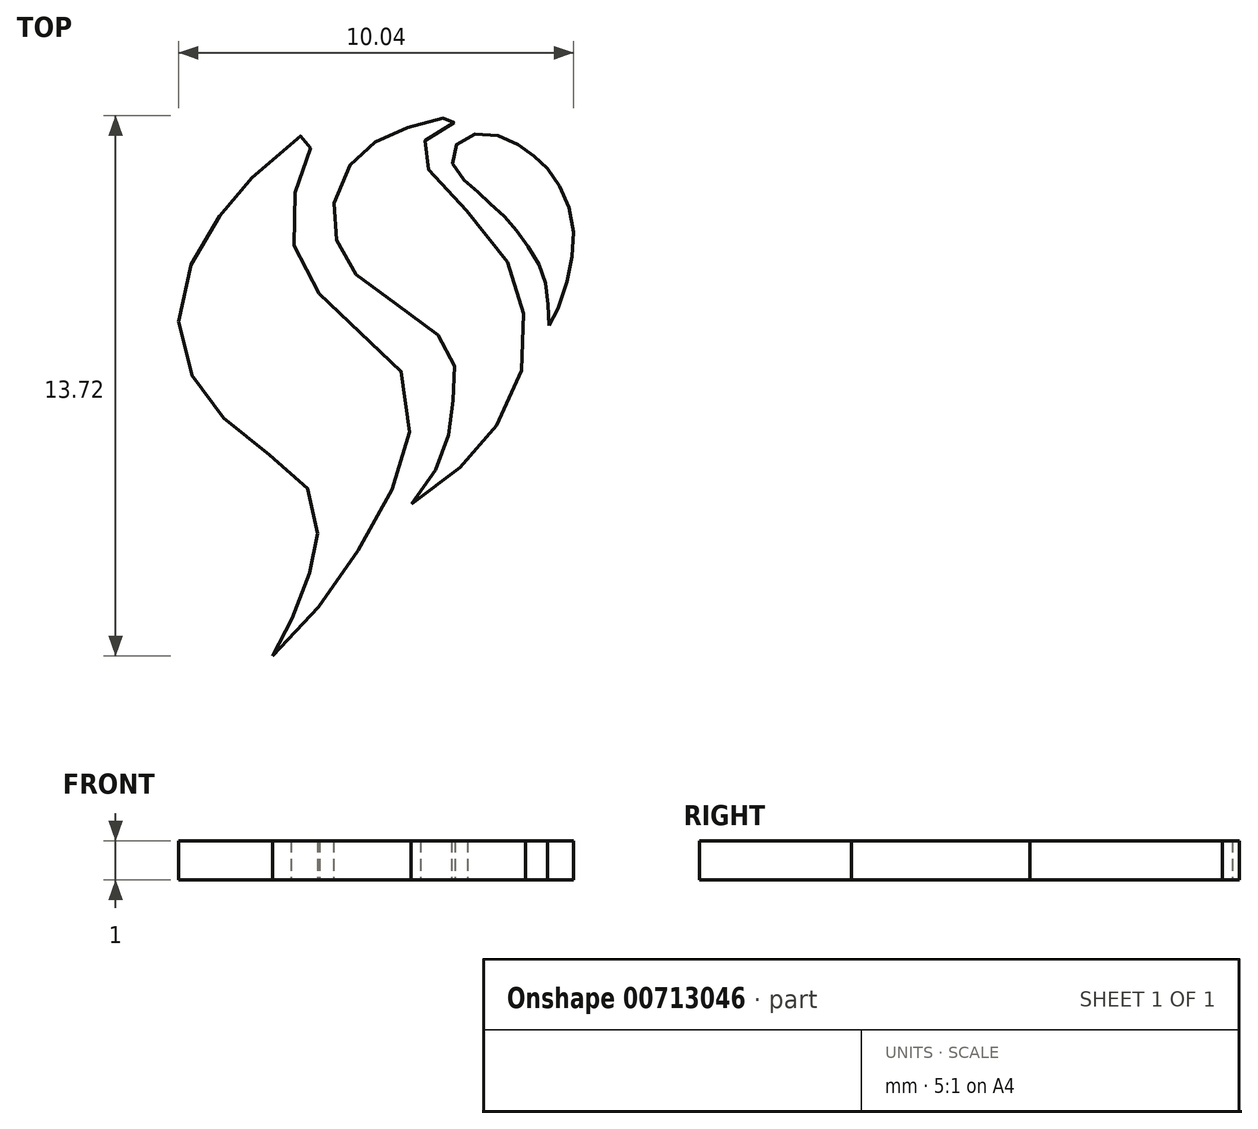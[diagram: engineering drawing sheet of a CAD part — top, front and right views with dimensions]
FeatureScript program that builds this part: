
annotation { "Feature Type Name" : "Feature", "Feature Type Description" : "" }
export const myFeature = defineFeature(function(context is Context, id is Id, definition is map)
    precondition{}
    {
        {
            var Q0;
            Q0=qCreatedBy(makeId("Top.planeOp"),FACE);
            var sketch = newSketch(context, id + "F0", { "sketchPlane" : qUnion([Q0])});
            skFitSpline(sketch, "E0", {"points": [v(-1.7, -8.38) * mm, v(-1.5, -8.04) * mm, v(-1.34, -7.68) * mm, v(-1.1, -7.2) * mm, v(-0.86, -6.51) * mm, v(-0.77, -6.27) * mm, v(-0.66, -5.92) * mm, v(-0.58, -5.52) * mm, v(-0.56, -5.15) * mm, v(-0.6, -4.61) * mm, v(-0.8, -4.16) * mm, v(-1.21, -3.7) * mm, v(-1.66, -3.36) * mm, v(-2.33, -2.9) * mm, v(-2.92, -2.38) * mm, v(-3.34, -1.9) * mm, v(-3.72, -1.33) * mm, v(-3.96, -0.8) * mm, v(-4.1, 0) * mm, v(-4.04, 0.84) * mm, v(-3.77, 1.58) * mm, v(-3.4, 2.33) * mm, v(-3.04, 2.82) * mm, v(-2.69, 3.24) * mm, v(-2.27, 3.72) * mm, v(-1.86, 4.11) * mm, v(-0.9, 4.9) * mm, v(-0.52, 5.14) * mm, v(-0.7, 4.61) * mm, v(-0.85, 4.23) * mm, v(-1.07, 3.65) * mm, v(-1.18, 3.15) * mm, v(-1.23, 2.49) * mm, v(-1.08, 1.76) * mm, v(-0.8, 1.16) * mm, v(-0.35, 0.63) * mm, v(0.08, 0.16) * mm, v(0.83, -0.38) * mm, v(1.32, -0.81) * mm, v(1.73, -1.55) * mm, v(1.8, -2.43) * mm, v(1.63, -3.32) * mm, v(1.36, -4.06) * mm, v(0.88, -5) * mm, v(0.28, -5.99) * mm, v(-0.32, -6.84) * mm, v(-1.24, -7.97) * mm, v(-1.7, -8.38) * mm]});
            skFitSpline(sketch, "E1", {"points": [v(1.82, -4.52) * mm, v(2.2, -4.06) * mm, v(2.43, -3.65) * mm, v(2.6, -3.25) * mm, v(2.74, -2.83) * mm, v(2.8, -2.53) * mm, v(2.85, -2.15) * mm, v(2.9, -1.7) * mm, v(2.9, -1.27) * mm, v(2.92, -1) * mm, v(2.78, -0.64) * mm, v(2.55, -0.3) * mm, v(2.25, 0) * mm, v(1.32, 0.63) * mm, v(0.69, 1.05) * mm, v(0.26, 1.5) * mm, v(0.01, 1.96) * mm, v(-0.11, 2.27) * mm, v(-0.16, 2.72) * mm, v(-0.14, 3.15) * mm, v(0, 3.72) * mm, v(0.28, 4.11) * mm, v(0.5, 4.34) * mm, v(0.82, 4.61) * mm, v(1.09, 4.78) * mm, v(1.54, 4.96) * mm, v(1.8, 5.07) * mm, v(2.32, 5.2) * mm, v(2.65, 5.28) * mm, v(3.24, 5.33) * mm, v(2.93, 5.19) * mm, v(2.57, 5) * mm, v(2.28, 4.8) * mm, v(2.08, 4.6) * mm, v(2.07, 4.27) * mm, v(2.25, 3.98) * mm, v(2.6, 3.55) * mm, v(3.7, 2.44) * mm, v(4.31, 1.51) * mm, v(4.6, 0.7) * mm, v(4.71, -0.4) * mm, v(4.57, -1.31) * mm, v(4.1, -2.36) * mm, v(3.42, -3.21) * mm, v(2.74, -3.89) * mm, v(1.82, -4.52) * mm]});
            skFitSpline(sketch, "E2", {"points": [v(5.3, 0) * mm, v(5.6, 0.56) * mm, v(5.85, 1.54) * mm, v(5.94, 2.4) * mm, v(5.75, 3.2) * mm, v(5.4, 3.84) * mm, v(5.07, 4.2) * mm, v(4.66, 4.52) * mm, v(4.08, 4.82) * mm, v(3.36, 4.86) * mm, v(2.89, 4.5) * mm, v(2.93, 3.96) * mm, v(3.33, 3.56) * mm, v(3.61, 3.29) * mm, v(3.94, 3) * mm, v(4.32, 2.63) * mm, v(4.6, 2.26) * mm, v(4.95, 1.76) * mm, v(5.18, 1.22) * mm, v(5.28, 0.7) * mm, v(5.3, 0) * mm]});
            skSolve(sketch);
        }
        {
            var Q0;
            Q0=makeQuery(id+"F0.imprint","IMPRINT",FACE,{"disambiguationData":[TD([[makeQuery(id+"F0.imprint","IMPRINT",EDGE,{"derivedFrom":sQuery(id+"F0.wireOp",EDGE,"E0")}),-1.0]])]});
            var Q1;
            Q1=makeQuery(id+"F0.imprint","IMPRINT",FACE,{"disambiguationData":[TD([[makeQuery(id+"F0.imprint","IMPRINT",EDGE,{"derivedFrom":sQuery(id+"F0.wireOp",EDGE,"E1")}),-1.0]])]});
            var Q2;
            Q2=makeQuery(id+"F0.imprint","IMPRINT",FACE,{"disambiguationData":[TD([[makeQuery(id+"F0.imprint","IMPRINT",EDGE,{"derivedFrom":sQuery(id+"F0.wireOp",EDGE,"E2")}),1.0]])]});
            extrude(context, id + "F1", {"entities" : qUnion([Q0, Q1, Q2]), "depth" : 1 * mm, "offsetDistance" : 25 * mm});
        }
    });
